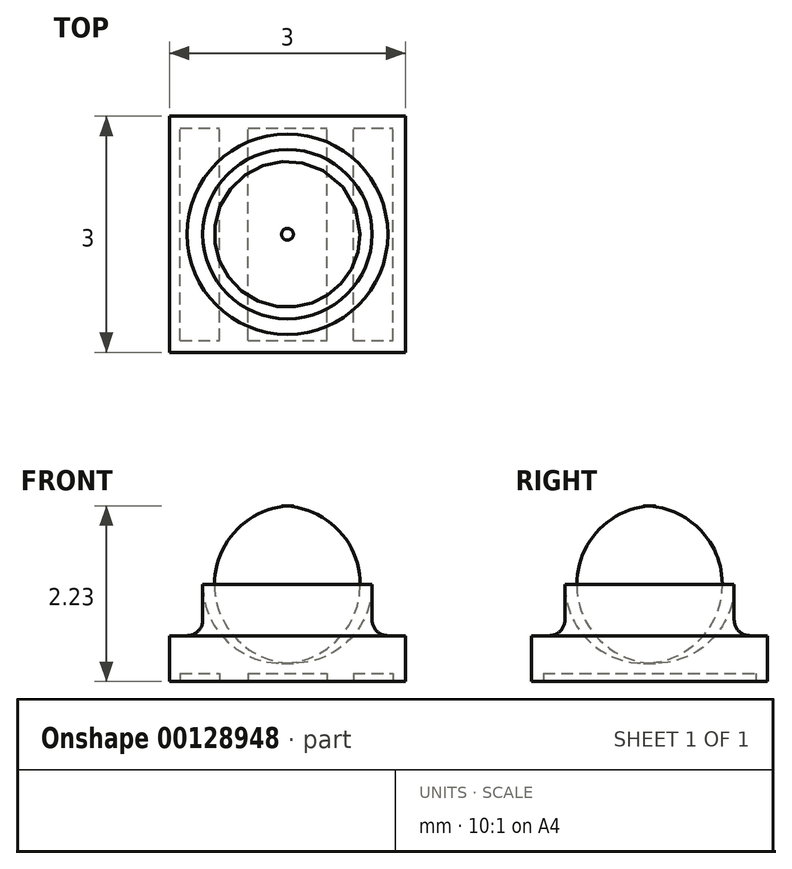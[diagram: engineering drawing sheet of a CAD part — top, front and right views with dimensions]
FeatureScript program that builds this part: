
annotation { "Feature Type Name" : "Feature", "Feature Type Description" : "" }
export const myFeature = defineFeature(function(context is Context, id is Id, definition is map)
    precondition{}
    {
        {
            var Q0;
            Q0=qCreatedBy(makeId("Top.planeOp"),FACE);
            var sketch = newSketch(context, id + "F0", { "sketchPlane" : qUnion([Q0])});
            skLineSegment(sketch, "E0.bottom", {"start": v(-1.5, 1.5) * mm, "end": v(1.5, 1.5) * mm});
            skLineSegment(sketch, "E0.top", {"start": v(-1.5, -1.5) * mm, "end": v(1.5, -1.5) * mm});
            skLineSegment(sketch, "E0.left", {"start": v(-1.5, 1.5) * mm, "end": v(-1.5, -1.5) * mm});
            skLineSegment(sketch, "E0.right", {"start": v(1.5, 1.5) * mm, "end": v(1.5, -1.5) * mm});
            skSolve(sketch);
        }
        {
            var Q0;
            Q0 = qSketchRegion(id + "F0", true);
            extrude(context, id + "F1", {"entities" : qUnion([Q0]), "depth" : .58 * mm});
        }
        {
            var Q0;
            Q0=qCreatedBy(makeId("Front.planeOp"),FACE);
            var sketch = newSketch(context, id + "F2", { "sketchPlane" : qUnion([Q0])});
            skLineSegment(sketch, "E1.right", {"start": v(1.07, 0.78) * mm, "end": v(1.07, 1.23) * mm});
            skArc(sketch, "E2.filletArc", {"start": v(1.07, 0.78) * mm, "mid": v(1.13, 0.64) * mm, "end": v(1.28, 0.58) * mm});
            skPoint(sketch, "E3.visualSharp", {"position": v(1.07, 2.23) * mm});
            skArc(sketch, "E3.filletArc", {"start": v(1.07, 1.23) * mm, "mid": v(0.78, 1.94) * mm, "end": v(0.08, 2.23) * mm});
            skLineSegment(sketch, "E4", {"start": v(0.08, 2.23) * mm, "end": v(0, 2.23) * mm});
            skLineSegment(sketch, "E5", {"start": v(1.28, 0.58) * mm, "end": v(0, 0.58) * mm});
            skLineSegment(sketch, "E6", {"start": v(0, 0.58) * mm, "end": v(0, 2.23) * mm});
            skSolve(sketch);
        }
        {
            var Q0;
            Q0 = qSketchRegion(id + "F2", true);
            var Q1;
            Q1=sQuery(id+"F2.wireOp",EDGE,"E6");
            revolve(context, id + "F3", {"entities" : qUnion([Q0]), "axis" : qUnion([Q1]), "revolveType" : RevolveType.FULL});
        }
        {
            var Q0;
            Q0=makeQuery(id+"F1.opExtrude","CAP_FACE",FACE,{"disambiguationData":[OSD([sQuery(id+"F0.wireOp",EDGE,"E0.bottom"),sQuery(id+"F0.wireOp",EDGE,"E0.top"),sQuery(id+"F0.wireOp",EDGE,"E0.left"),sQuery(id+"F0.wireOp",EDGE,"E0.right")])],"isStart":true});
            var sketch = newSketch(context, id + "F4", { "sketchPlane" : qUnion([Q0])});
            skLineSegment(sketch, "E7.bottom", {"start": v(-0.5, 1.35) * mm, "end": v(0.5, 1.35) * mm});
            skLineSegment(sketch, "E7.top", {"start": v(-0.5, -1.35) * mm, "end": v(0.5, -1.35) * mm});
            skLineSegment(sketch, "E7.left", {"start": v(-0.5, 1.35) * mm, "end": v(-0.5, -1.35) * mm});
            skLineSegment(sketch, "E7.right", {"start": v(0.5, 1.35) * mm, "end": v(0.5, -1.35) * mm});
            skLineSegment(sketch, "E8.bottom", {"start": v(0.84, 1.35) * mm, "end": v(1.34, 1.35) * mm});
            skLineSegment(sketch, "E8.top", {"start": v(0.84, -1.35) * mm, "end": v(1.34, -1.35) * mm});
            skLineSegment(sketch, "E8.left", {"start": v(0.84, 1.35) * mm, "end": v(0.84, -1.35) * mm});
            skLineSegment(sketch, "E8.right", {"start": v(1.34, 1.35) * mm, "end": v(1.34, -1.35) * mm});
            skLineSegment(sketch, "E9.bottom", {"start": v(-1.36, 1.35) * mm, "end": v(-0.86, 1.35) * mm});
            skLineSegment(sketch, "E9.top", {"start": v(-1.36, -1.35) * mm, "end": v(-0.86, -1.35) * mm});
            skLineSegment(sketch, "E9.left", {"start": v(-1.36, 1.35) * mm, "end": v(-1.36, -1.35) * mm});
            skLineSegment(sketch, "E9.right", {"start": v(-0.86, 1.35) * mm, "end": v(-0.86, -1.35) * mm});
            skSolve(sketch);
        }
        {
            var Q0;
            Q0 = qSketchRegion(id + "F4", true);
            extrude(context, id + "F5", {"entities" : qUnion([Q0]), "operationType" : NewBodyOperationType.REMOVE, "oppositeDirection" : true, "depth" : .1 * mm});
        }
        {
            var Q0;
            Q0 = qSketchRegion(id + "F4", true);
            extrude(context, id + "F6", {"entities" : qUnion([Q0]), "oppositeDirection" : true, "depth" : .1 * mm});
        }
    });
